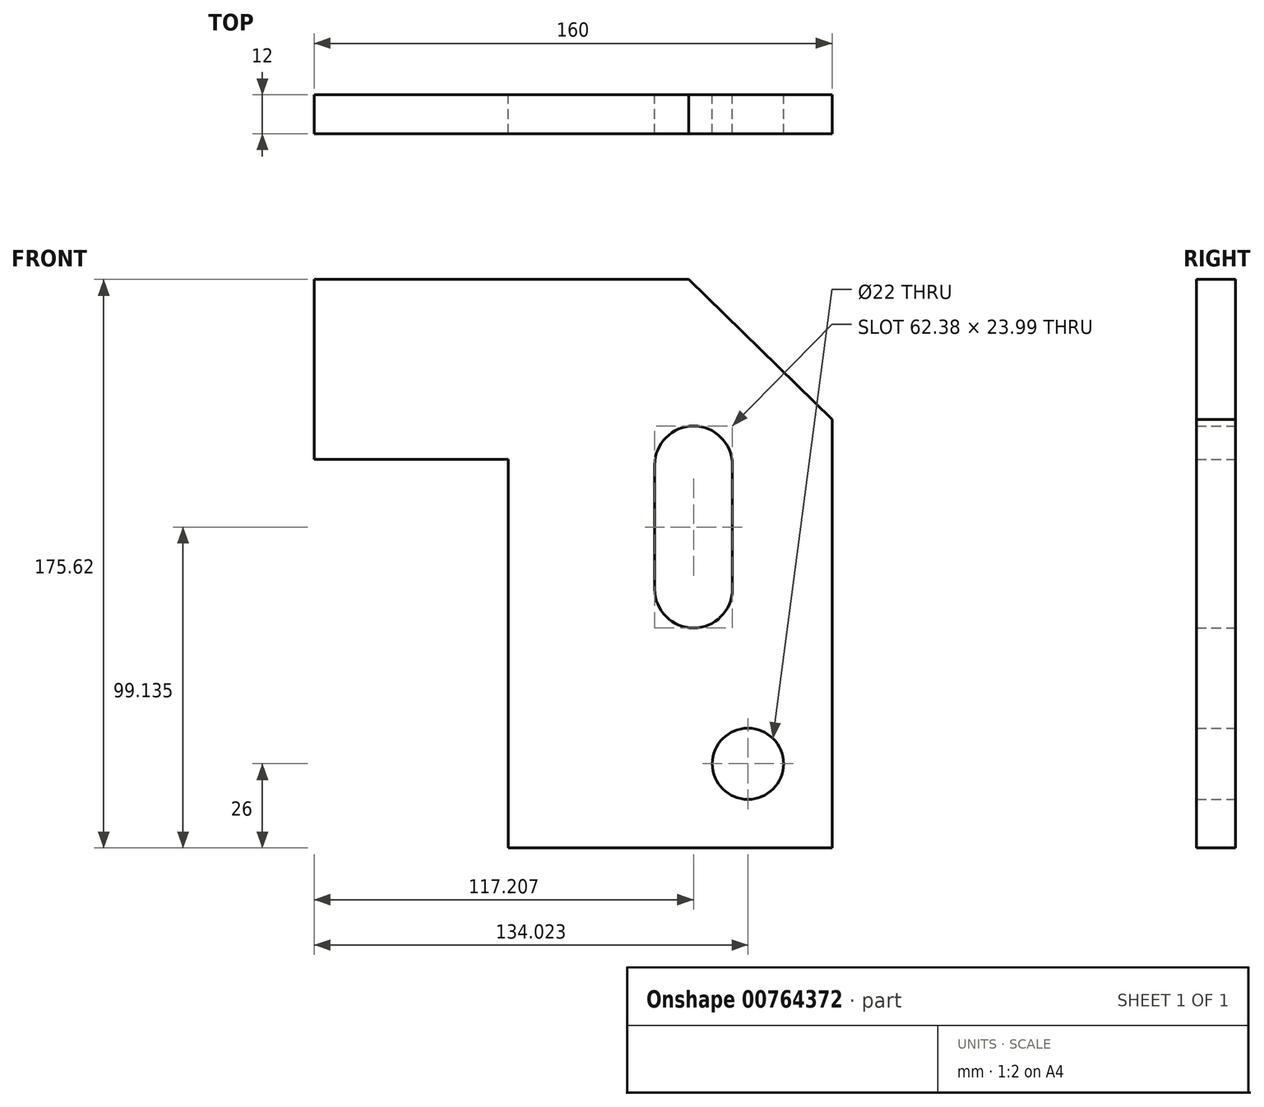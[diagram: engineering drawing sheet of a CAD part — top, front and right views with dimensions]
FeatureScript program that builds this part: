
annotation { "Feature Type Name" : "Feature", "Feature Type Description" : "" }
export const myFeature = defineFeature(function(context is Context, id is Id, definition is map)
    precondition{}
    {
        {
            var Q0;
            Q0=qCreatedBy(makeId("Front.planeOp"),FACE);
            var sketch = newSketch(context, id + "F0", { "sketchPlane" : qUnion([Q0])});
            skLineSegment(sketch, "E0.MirrorCS", {"start": v(19.08, 77.74) * mm, "end": v(-96.64, 77.74) * mm});
            skLineSegment(sketch, "E1.MirrorCS", {"start": v(63.36, -97.88) * mm, "end": v(-36.64, -97.88) * mm});
            skLineSegment(sketch, "E2.MirrorCS", {"start": v(-96.64, 77.74) * mm, "end": v(-96.64, 22.12) * mm});
            skLineSegment(sketch, "E3", {"start": v(19.08, 77.74) * mm, "end": v(63.36, 34.5) * mm});
            skLineSegment(sketch, "E4", {"start": v(63.36, 34.5) * mm, "end": v(63.36, -97.88) * mm});
            skCircle(sketch, "E5", {"center": v(37.38, -71.88) * mm, "radius": 11 * mm});
            skArc(sketch, "E6", {"start": v(32.56, 20.45) * mm, "mid": v(20.57, 32.45) * mm, "end": v(8.57, 20.45) * mm});
            skArc(sketch, "E7", {"start": v(8.57, -17.94) * mm, "mid": v(20.57, -29.94) * mm, "end": v(32.56, -17.94) * mm});
            skLineSegment(sketch, "E8", {"start": v(-36.64, -97.88) * mm, "end": v(-36.64, 22.12) * mm});
            skLineSegment(sketch, "E9", {"start": v(-36.64, 22.12) * mm, "end": v(-96.64, 22.12) * mm});
            skLineSegment(sketch, "E10", {"start": v(32.56, 20.45) * mm, "end": v(32.56, -17.94) * mm});
            skLineSegment(sketch, "E11", {"start": v(8.57, -17.94) * mm, "end": v(8.57, 20.45) * mm});
            skSolve(sketch);
        }
        {
            var Q0;
            Q0=makeQuery(id+"F0.imprint","IMPRINT",FACE,{"disambiguationData":[TD([[makeQuery(id+"F0.imprint","IMPRINT",EDGE,{"derivedFrom":sQuery(id+"F0.wireOp",EDGE,"E0.MirrorCS")}),1.0]])]});
            extrude(context, id + "F1", {"entities" : qUnion([Q0]), "depth" : 12 * mm, "offsetDistance" : 25 * mm});
        }
    });
